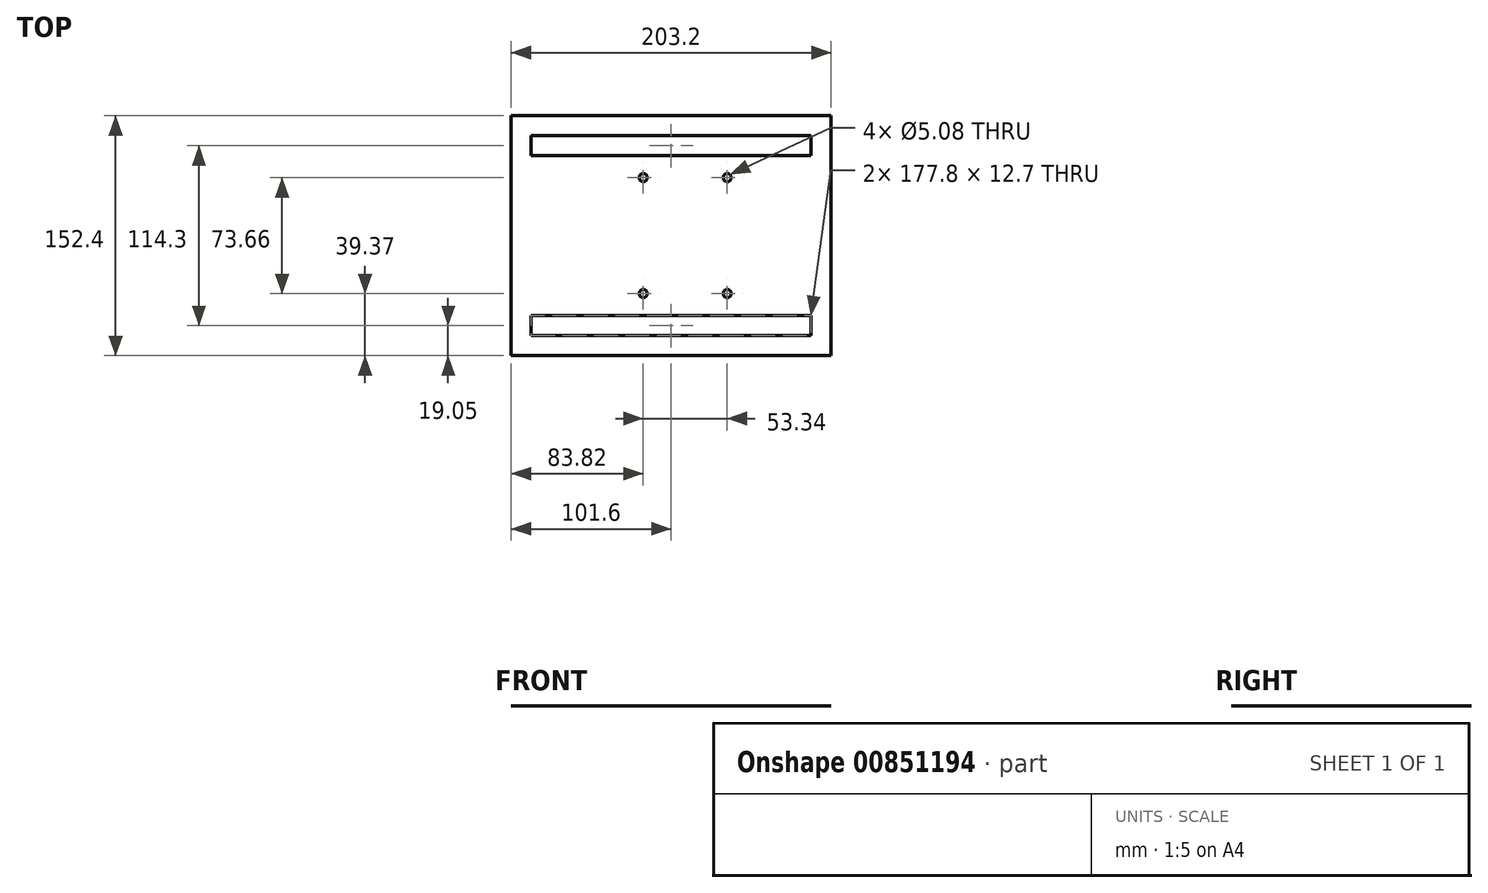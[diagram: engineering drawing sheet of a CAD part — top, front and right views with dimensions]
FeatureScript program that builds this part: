
annotation { "Feature Type Name" : "Feature", "Feature Type Description" : "" }
export const myFeature = defineFeature(function(context is Context, id is Id, definition is map)
    precondition{}
    {
        {
            var Q0;
            Q0=qCreatedBy(makeId("Top.planeOp"),FACE);
            var sketch = newSketch(context, id + "F0", { "sketchPlane" : qUnion([Q0])});
            skLineSegment(sketch, "E0.bottom", {"start": v(101.6, -76.2) * mm, "end": v(-101.6, -76.2) * mm});
            skLineSegment(sketch, "E0.top", {"start": v(101.6, 76.2) * mm, "end": v(-101.6, 76.2) * mm});
            skLineSegment(sketch, "E0.left", {"start": v(101.6, -76.2) * mm, "end": v(101.6, 76.2) * mm});
            skLineSegment(sketch, "E0.right", {"start": v(-101.6, -76.2) * mm, "end": v(-101.6, 76.2) * mm});
            skPoint(sketch, "E0.middle", {"position": v(0, 0) * mm});
            skLineSegment(sketch, "E1", {"start": v(-101.6, 50.8) * mm, "end": v(-101.6, 76.2) * mm, "construction": true});
            skLineSegment(sketch, "E2", {"start": v(-101.6, -76.2) * mm, "end": v(-101.6, -50.8) * mm, "construction": true});
            skLineSegment(sketch, "E3", {"start": v(-101.6, -50.8) * mm, "end": v(-88.9, -50.8) * mm, "construction": true});
            skLineSegment(sketch, "E4", {"start": v(-88.9, -50.8) * mm, "end": v(88.9, -50.8) * mm});
            skLineSegment(sketch, "E5", {"start": v(88.9, -50.8) * mm, "end": v(88.9, -63.5) * mm});
            skLineSegment(sketch, "E6", {"start": v(88.9, -63.5) * mm, "end": v(-88.9, -63.5) * mm});
            skLineSegment(sketch, "E7", {"start": v(-88.9, -63.5) * mm, "end": v(-88.9, -50.8) * mm});
            skLineSegment(sketch, "E8", {"start": v(-101.6, 50.8) * mm, "end": v(-88.9, 50.8) * mm, "construction": true});
            skLineSegment(sketch, "E9", {"start": v(-88.9, 50.8) * mm, "end": v(-88.9, 63.5) * mm});
            skLineSegment(sketch, "E10", {"start": v(-88.9, 63.5) * mm, "end": v(88.9, 63.5) * mm});
            skLineSegment(sketch, "E11", {"start": v(88.9, 63.5) * mm, "end": v(88.9, 50.8) * mm});
            skLineSegment(sketch, "E12", {"start": v(88.9, 50.8) * mm, "end": v(-88.9, 50.8) * mm});
            skLineSegment(sketch, "E13", {"start": v(0, 50.8) * mm, "end": v(0, 36.83) * mm, "construction": true});
            skLineSegment(sketch, "E14", {"start": v(0, 36.83) * mm, "end": v(35.56, 36.83) * mm, "construction": true});
            skLineSegment(sketch, "E15", {"start": v(0, 36.83) * mm, "end": v(-17.78, 36.83) * mm, "construction": true});
            skCircle(sketch, "E16", {"center": v(35.56, 36.83) * mm, "radius": 2.54 * mm});
            skCircle(sketch, "E17", {"center": v(-17.78, 36.83) * mm, "radius": 2.54 * mm});
            skLineSegment(sketch, "E18", {"start": v(0, -50.8) * mm, "end": v(0, -36.83) * mm, "construction": true});
            skLineSegment(sketch, "E19", {"start": v(0, -36.83) * mm, "end": v(35.56, -36.83) * mm, "construction": true});
            skLineSegment(sketch, "E20", {"start": v(0, -36.83) * mm, "end": v(-17.78, -36.83) * mm, "construction": true});
            skCircle(sketch, "E21", {"center": v(-17.78, -36.83) * mm, "radius": 2.54 * mm});
            skCircle(sketch, "E22", {"center": v(35.56, -36.83) * mm, "radius": 2.54 * mm});
            skLineSegment(sketch, "E23", {"start": v(-101.6, 0) * mm, "end": v(101.6, 0) * mm, "construction": true});
            skSolve(sketch);
        }
        {
            var Q0;
            Q0=makeQuery(id+"F0.imprint","IMPRINT",FACE,{"disambiguationData":[TD([[makeQuery(id+"F0.imprint","IMPRINT",EDGE,{"derivedFrom":sQuery(id+"F0.wireOp",EDGE,"Ln5NRlxT-onw6-Xl1H-iI2w-PTsChE4MnZd7.bottom")}),-1.0]])]});
            var Q1;
            Q1=makeQuery(id+"F0.imprint","IMPRINT",FACE,{"disambiguationData":[TD([[makeQuery(id+"F0.imprint","IMPRINT",EDGE,{"derivedFrom":sQuery(id+"F0.wireOp",EDGE,"E0.bottom")}),-1.0]])]});
            extrude(context, id + "F1", {"entities" : qUnion([Q0, Q1]), "depth" : 1 / 203.2 * mm, "offsetDistance" : 25.4 * mm});
        }
    });
